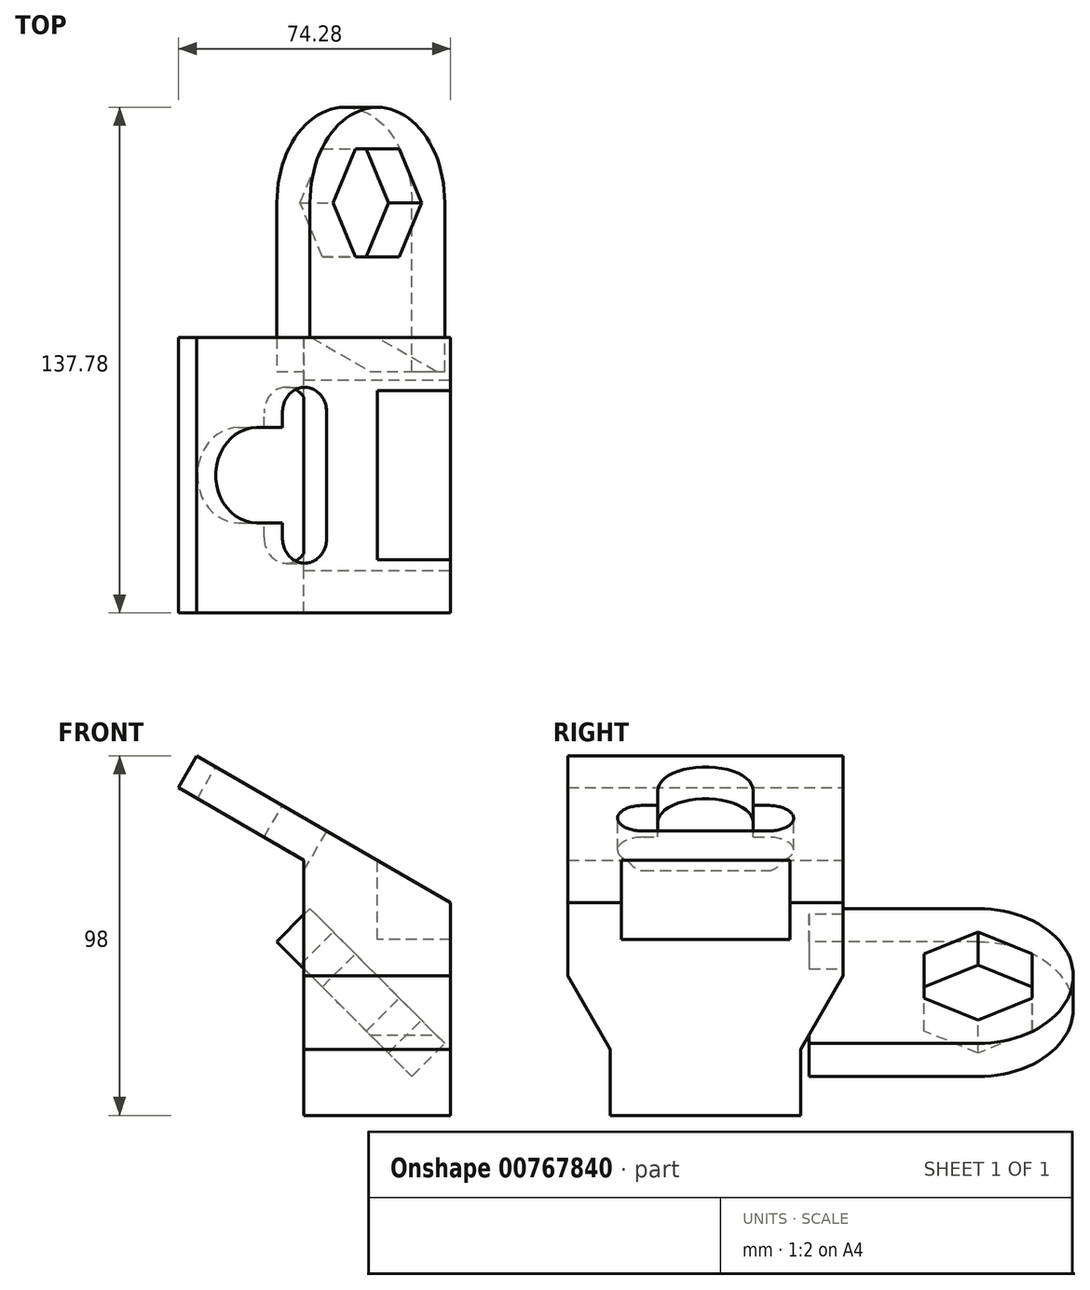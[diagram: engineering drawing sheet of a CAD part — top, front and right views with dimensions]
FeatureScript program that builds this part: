
annotation { "Feature Type Name" : "Feature", "Feature Type Description" : "" }
export const myFeature = defineFeature(function(context is Context, id is Id, definition is map)
    precondition{}
    {
        {
            var Q0;
            Q0=qCreatedBy(makeId("Front.planeOp"),FACE);
            var sketch = newSketch(context, id + "F0", { "sketchPlane" : qUnion([Q0])});
            skLineSegment(sketch, "E0", {"start": v(0, -20) * mm, "end": v(0, 0) * mm});
            skLineSegment(sketch, "E1", {"start": v(0, 0) * mm, "end": v(-69.28, 40) * mm});
            skLineSegment(sketch, "E2", {"start": v(-69.28, 40) * mm, "end": v(-74.28, 31.34) * mm});
            skLineSegment(sketch, "E3", {"start": v(-74.28, 31.34) * mm, "end": v(-40, 11.55) * mm});
            skLineSegment(sketch, "E4", {"start": v(-40, 11.55) * mm, "end": v(-40, -20) * mm});
            skLineSegment(sketch, "E5", {"start": v(-40, -20) * mm, "end": v(0, -20) * mm});
            skLineSegment(sketch, "E6", {"start": v(0, -10) * mm, "end": v(-20, -10) * mm});
            skLineSegment(sketch, "E7", {"start": v(-20, -10) * mm, "end": v(-20, 11.55) * mm});
            skSolve(sketch);
        }
        {
            var Q0;
            Q0 = qSketchRegion(id + "F0", true);
            extrude(context, id + "F1", {"entities" : qUnion([Q0]), "depth" : 75 * mm, "offsetDistance" : 25 * mm, "symmetric" : true});
        }
        {
            var Q0;
            {var subQ3=sQuery(id+"F0.wireOp",EDGE,"E6");Q0=makeQuery(id+"F0.imprint","IMPRINT",FACE,{"disambiguationData":[TD([[makeQuery(id+"F0.imprint","IMPRINT",EDGE,{"derivedFrom":subQ3}),-1.0]])]});}
            extrude(context, id + "F2", {"entities" : qUnion([Q0]), "operationType" : NewBodyOperationType.REMOVE, "oppositeDirection" : true, "depth" : 46 * mm, "offsetDistance" : 25 * mm, "symmetric" : true});
        }
        {
            var Q0;
            Q0=qCreatedBy(makeId("Right.planeOp"),FACE);
            var sketch = newSketch(context, id + "F3", { "sketchPlane" : qUnion([Q0])});
            skLineSegment(sketch, "E8", {"start": v(0, 0) * mm, "end": v(0, -24.65) * mm, "construction": true});
            skLineSegment(sketch, "E9.0", {"start": v(-37.5, -20) * mm, "end": v(37.5, -20) * mm});
            skLineSegment(sketch, "E10", {"start": v(-37.5, -20) * mm, "end": v(-26, -40) * mm});
            skLineSegment(sketch, "E11", {"start": v(-26, -40) * mm, "end": v(-26, -58) * mm});
            skLineSegment(sketch, "E12", {"start": v(-26, -58) * mm, "end": v(0, -58) * mm});
            skLineSegment(sketch, "E13.MirrorCS", {"start": v(37.5, -20) * mm, "end": v(26, -40) * mm});
            skLineSegment(sketch, "E14.MirrorCS", {"start": v(26, -40) * mm, "end": v(26, -58) * mm});
            skLineSegment(sketch, "E15.MirrorCS", {"start": v(26, -58) * mm, "end": v(0, -58) * mm});
            skLineSegment(sketch, "E16", {"start": v(-26, -40) * mm, "end": v(26, -40) * mm});
            skSolve(sketch);
        }
        {
            var Q0;
            Q0 = qSketchRegion(id + "F3", true);
            extrude(context, id + "F4", {"entities" : qUnion([Q0]), "operationType" : NewBodyOperationType.ADD, "oppositeDirection" : true, "depth" : 40 * mm, "offsetDistance" : 25 * mm});
        }
        {
            var Q0;
            Q0=sQuery(id+"F3.wireOp",EDGE,"E16");
            cPlane(context, id + "F5", {"entities" : qUnion([Q0]), "cplaneType" : CPlaneType.LINE_ANGLE, "offset" : 25 * mm, "angle" : 45 * degree, "width" : 150 * mm, "height" : 150 * mm});
        }
        {
            var Q0;
            Q0=qCreatedBy(id+"F5.planeOp",FACE);
            var sketch = newSketch(context, id + "F6", { "sketchPlane" : qUnion([Q0])});
            skLineSegment(sketch, "E17", {"start": v(28.28, 26) * mm, "end": v(28.28, -26) * mm});
            skLineSegment(sketch, "E18", {"start": v(28.28, -26) * mm, "end": v(74.28, -26) * mm});
            skLineSegment(sketch, "E19", {"start": v(74.28, 26) * mm, "end": v(28.28, 26) * mm});
            skArc(sketch, "E20", {"start": v(74.28, -26) * mm, "mid": v(100.28, 0) * mm, "end": v(74.28, 26) * mm});
            skCircle(sketch, "E21.cCircle", {"center": v(74.28, 0) * mm, "radius": 17 * mm, "construction": true});
            skLineSegment(sketch, "E21.0", {"start": v(74.28, 17) * mm, "end": v(89, 8.5) * mm});
            skLineSegment(sketch, "E21.1", {"start": v(89, 8.5) * mm, "end": v(89, -8.5) * mm});
            skLineSegment(sketch, "E21.2", {"start": v(89, -8.5) * mm, "end": v(74.28, -17) * mm});
            skLineSegment(sketch, "E21.3", {"start": v(74.28, -17) * mm, "end": v(59.56, -8.5) * mm});
            skLineSegment(sketch, "E21.4", {"start": v(59.56, -8.5) * mm, "end": v(59.56, 8.5) * mm});
            skLineSegment(sketch, "E21.5", {"start": v(59.56, 8.5) * mm, "end": v(74.28, 17) * mm});
            skSolve(sketch);
        }
        {
            var Q0;
            Q0 = qSketchRegion(id + "F6", true);
            var Q1;
            Q1=makeQuery(id+"F4.opExtrude","CAP_VERTEX",VERTEX,{"disambiguationData":[OSD([sQuery(id+"F3.wireOp",EDGE,"E11"),sQuery(id+"F3.wireOp",EDGE,"E12")])],"isStart":true});
            extrude(context, id + "F7", {"entities" : qUnion([Q0]), "operationType" : NewBodyOperationType.ADD, "endBound" : BoundingType.UP_TO_VERTEX, "oppositeDirection" : true, "depth" : 25 * mm, "endBoundEntityVertex" : qUnion([Q1]), "offsetDistance" : 25 * mm});
        }
        {
            var Q0;
            Q0=makeQuery(id+"F1.opExtrude","SWEPT_FACE",FACE,{"disambiguationData":[OSD([sQuery(id+"F0.wireOp",EDGE,"E1")])]});
            var sketch = newSketch(context, id + "F8", { "sketchPlane" : qUnion([Q0])});
            skLineSegment(sketch, "E22", {"start": v(-46, -17) * mm, "end": v(-46, 17) * mm, "construction": true});
            skLineSegment(sketch, "E23", {"start": v(0, 0) * mm, "end": v(-21.38, 0) * mm, "construction": true});
            skArc(sketch, "E24.0.startCap", {"start": v(-39, -17) * mm, "mid": v(-46, -24) * mm, "end": v(-53, -17) * mm});
            skArc(sketch, "E24.0.endCap", {"start": v(-53, 17) * mm, "mid": v(-46, 24) * mm, "end": v(-39, 17) * mm});
            skLineSegment(sketch, "E24.0.left", {"start": v(-53, -17) * mm, "end": v(-53, -13) * mm});
            skLineSegment(sketch, "E24.0.right", {"start": v(-39, -17) * mm, "end": v(-39, 17) * mm});
            skArc(sketch, "E25", {"start": v(-61, 13) * mm, "mid": v(-74, 0) * mm, "end": v(-61, -13) * mm});
            skPoint(sketch, "E25.centerSnap0", {"position": v(-53, 0) * mm});
            skLineSegment(sketch, "E26", {"start": v(-61, -13) * mm, "end": v(-53, -13) * mm});
            skLineSegment(sketch, "E27", {"start": v(-61, 13) * mm, "end": v(-53, 13) * mm});
            skLineSegment(sketch, "E28.trimOffspring", {"start": v(-53, 13) * mm, "end": v(-53, 17) * mm});
            skSolve(sketch);
        }
        {
            var Q0;
            Q0 = qSketchRegion(id + "F8", true);
            extrude(context, id + "F9", {"entities" : qUnion([Q0]), "operationType" : NewBodyOperationType.REMOVE, "endBound" : BoundingType.THROUGH_ALL, "oppositeDirection" : true, "depth" : 25 * mm, "offsetDistance" : 25 * mm});
        }
    });
